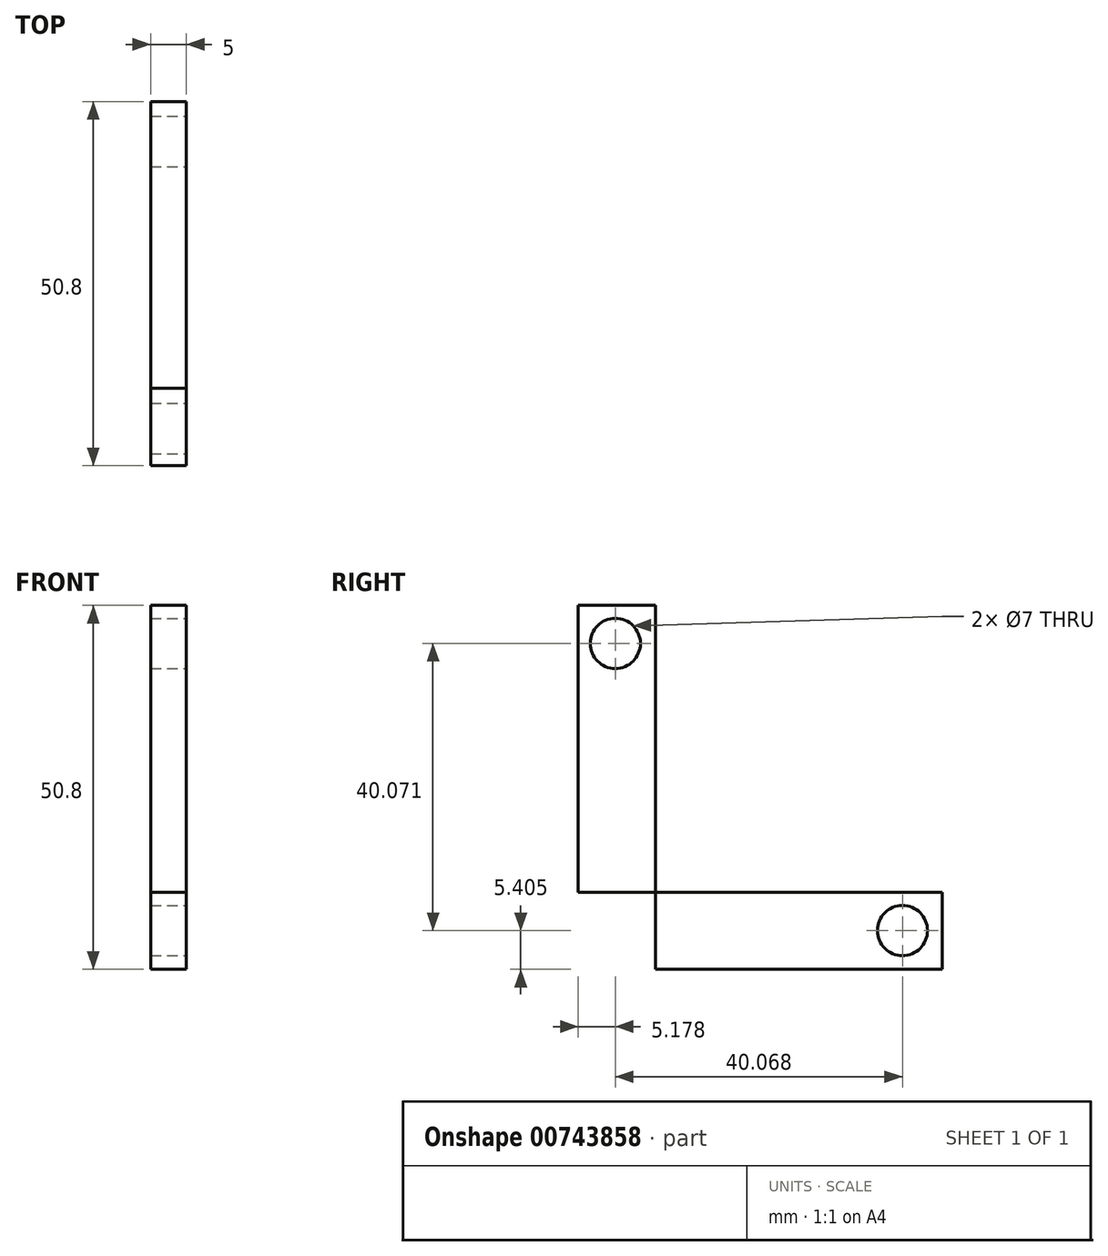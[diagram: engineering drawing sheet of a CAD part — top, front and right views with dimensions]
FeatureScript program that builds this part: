
annotation { "Feature Type Name" : "Feature", "Feature Type Description" : "" }
export const myFeature = defineFeature(function(context is Context, id is Id, definition is map)
    precondition{}
    {
        {
            var Q0;
            Q0=qCreatedBy(makeId("Right.planeOp"),FACE);
            var sketch = newSketch(context, id + "F0", { "sketchPlane" : qUnion([Q0])});
            skLineSegment(sketch, "E0.bottom", {"start": v(-30.1, 24.74) * mm, "end": v(-19.29, 24.74) * mm});
            skLineSegment(sketch, "E0.top", {"start": v(-30.1, -26.06) * mm, "end": v(-19.29, -26.06) * mm});
            skLineSegment(sketch, "E0.left", {"start": v(-30.1, 24.74) * mm, "end": v(-30.1, -26.06) * mm});
            skLineSegment(sketch, "E0.right", {"start": v(-19.29, 24.74) * mm, "end": v(-19.29, -26.06) * mm});
            skLineSegment(sketch, "E1.bottom", {"start": v(-30.1, -26.06) * mm, "end": v(20.7, -26.06) * mm});
            skLineSegment(sketch, "E1.top", {"start": v(-30.1, -15.32) * mm, "end": v(20.7, -15.32) * mm});
            skLineSegment(sketch, "E1.left", {"start": v(-30.1, -26.06) * mm, "end": v(-30.1, -15.32) * mm});
            skLineSegment(sketch, "E1.right", {"start": v(20.7, -26.06) * mm, "end": v(20.7, -15.32) * mm});
            skSolve(sketch);
        }
        {
            var Q0;
            {var subQ0=sQuery(id+"F0.wireOp",EDGE,"E0.bottom");Q0=makeQuery(id+"F0.imprint","IMPRINT",FACE,{"disambiguationData":[TD([[makeQuery(id+"F0.imprint","IMPRINT",EDGE,{"derivedFrom":subQ0}),-1.0]])]});}
            var Q1;
            {var subQ5=sQuery(id+"F0.wireOp",EDGE,"E1.left");Q1=makeQuery(id+"F0.imprint","IMPRINT",FACE,{"disambiguationData":[TD([[makeQuery(id+"F0.imprint","IMPRINT",EDGE,{"derivedFrom":subQ5}),-1.0]])]});}
            var Q2;
            {var subQ5=sQuery(id+"F0.wireOp",EDGE,"E1.right");Q2=makeQuery(id+"F0.imprint","IMPRINT",FACE,{"disambiguationData":[TD([[makeQuery(id+"F0.imprint","IMPRINT",EDGE,{"derivedFrom":subQ5}),1.0]])]});}
            extrude(context, id + "F1", {"entities" : qUnion([Q0, Q1, Q2]), "depth" : 5 * mm, "offsetDistance" : 25.4 * mm});
        }
        {
            var Q0;
            Q0=makeQuery(id+"F1.opExtrude","CAP_FACE",FACE,{"disambiguationData":[OSD([sQuery(id+"F0.wireOp",EDGE,"E0.bottom"),sQuery(id+"F0.wireOp",EDGE,"E0.left"),sQuery(id+"F0.wireOp",EDGE,"E0.right"),sQuery(id+"F0.wireOp",EDGE,"E1.bottom"),sQuery(id+"F0.wireOp",EDGE,"E1.top"),sQuery(id+"F0.wireOp",EDGE,"E1.left"),sQuery(id+"F0.wireOp",EDGE,"E1.right")])],"isStart":false});
            var sketch = newSketch(context, id + "F2", { "sketchPlane" : qUnion([Q0])});
            skCircle(sketch, "E2", {"center": v(-24.91, 19.42) * mm, "radius": 3.5 * mm});
            skCircle(sketch, "E3", {"center": v(-24.55, -18.82) * mm, "radius": 3.5 * mm});
            skCircle(sketch, "E4", {"center": v(15.16, -20.65) * mm, "radius": 3.5 * mm});
            skSolve(sketch);
        }
        {
            var Q0;
            Q0=makeQuery(id+"F2.imprint","IMPRINT",FACE,{"disambiguationData":[TD([[makeQuery(id+"F2.imprint","IMPRINT",EDGE,{"derivedFrom":sQuery(id+"F2.wireOp",EDGE,"E2")}),1.0]])]});
            var Q1;
            Q1=makeQuery(id+"F2.imprint","IMPRINT",FACE,{"disambiguationData":[TD([[makeQuery(id+"F2.imprint","IMPRINT",EDGE,{"derivedFrom":sQuery(id+"F2.wireOp",EDGE,"E4")}),1.0]])]});
            var Q2;
            Q2=makeQuery(id+"F2.imprint","IMPRINT",FACE,{"disambiguationData":[TD([[makeQuery(id+"F2.imprint","IMPRINT",EDGE,{"derivedFrom":sQuery(id+"F2.wireOp",EDGE,"E3")}),1.0]])]});
            extrude(context, id + "F3", {"entities" : qUnion([Q0, Q1, Q2]), "operationType" : NewBodyOperationType.REMOVE, "oppositeDirection" : true, "depth" : 25.4 * mm, "offsetDistance" : 25.4 * mm});
        }
    });
